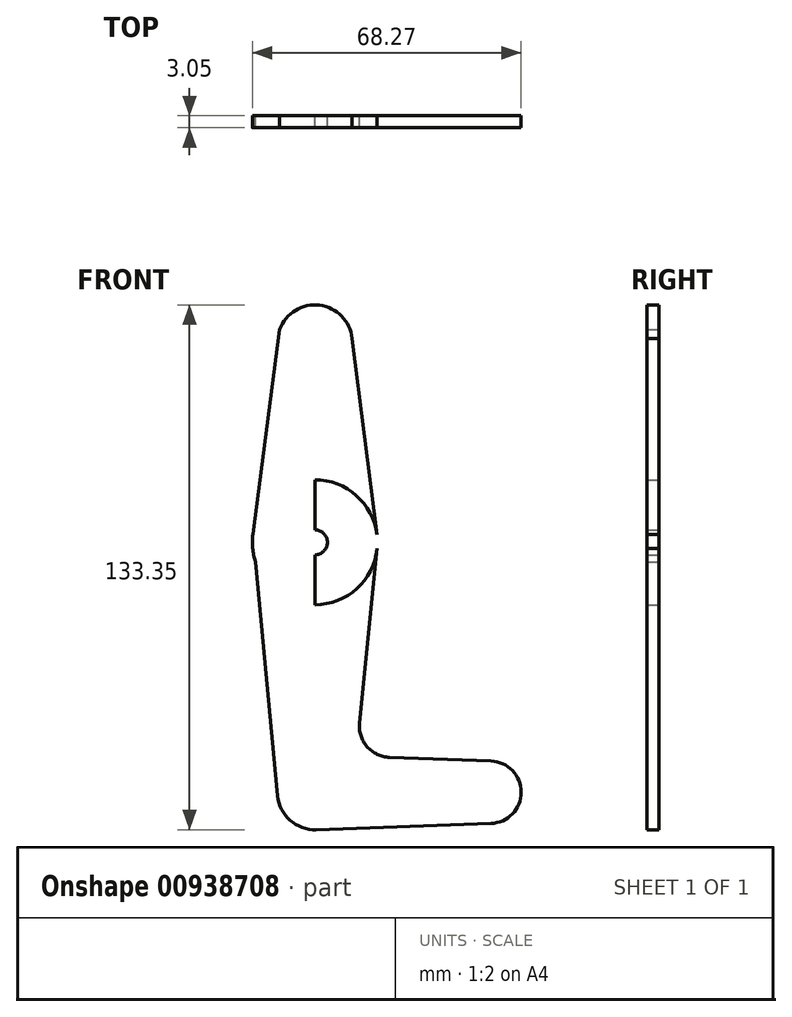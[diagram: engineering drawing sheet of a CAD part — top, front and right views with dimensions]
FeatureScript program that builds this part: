
annotation { "Feature Type Name" : "Feature", "Feature Type Description" : "" }
export const myFeature = defineFeature(function(context is Context, id is Id, definition is map)
    precondition{}
    {
        {
            var Q0;
            Q0=qCreatedBy(makeId("Front.planeOp"),FACE);
            var sketch = newSketch(context, id + "F0", { "sketchPlane" : qUnion([Q0])});
            skLineSegment(sketch, "E0", {"start": v(-32.72, 73.87) * mm, "end": v(-32.72, -40.43) * mm});
            skLineSegment(sketch, "E1", {"start": v(-32.72, -40.43) * mm, "end": v(11.73, -40.43) * mm});
            skCircle(sketch, "E2", {"center": v(-32.72, 73.87) * mm, "radius": 9.53 * mm});
            skCircle(sketch, "E3", {"center": v(-32.72, 23.07) * mm, "radius": 15.88 * mm});
            skCircle(sketch, "E4", {"center": v(-32.72, -40.43) * mm, "radius": 9.53 * mm});
            skCircle(sketch, "E5", {"center": v(11.73, -40.43) * mm, "radius": 7.94 * mm});
            skLineSegment(sketch, "E6", {"start": v(-16.92, 21.48) * mm, "end": v(-21.38, -22.84) * mm});
            skLineSegment(sketch, "E7", {"start": v(-32.38, -49.95) * mm, "end": v(12.01, -48.37) * mm});
            skLineSegment(sketch, "E8", {"start": v(-41.65, 77.18) * mm, "end": v(-48.46, 25.13) * mm});
            skLineSegment(sketch, "E9", {"start": v(-48.46, 25.13) * mm, "end": v(-42.2, -41.33) * mm});
            skLineSegment(sketch, "E10", {"start": v(-23.25, 74.86) * mm, "end": v(-16.97, 25.05) * mm});
            skLineSegment(sketch, "E11", {"start": v(-13.75, -31.58) * mm, "end": v(12.01, -32.5) * mm});
            skArc(sketch, "E12.filletArc", {"start": v(-21.38, -22.84) * mm, "mid": v(-19.46, -28.86) * mm, "end": v(-13.75, -31.58) * mm});
            skCircle(sketch, "E13", {"center": v(-32.72, 73.87) * mm, "radius": 3.18 * mm});
            skCircle(sketch, "E14", {"center": v(-32.72, 23.07) * mm, "radius": 3.18 * mm});
            skCircle(sketch, "E15", {"center": v(-32.72, -40.43) * mm, "radius": 3.18 * mm});
            skCircle(sketch, "E16", {"center": v(11.73, -40.43) * mm, "radius": 3.17 * mm});
            skCircle(sketch, "E17", {"center": v(-35.9, 59.6) * mm, "radius": 3.18 * mm});
            skSolve(sketch);
        }
        {
            var Q0;
            {var subQ0=sQuery(id+"F0.wireOp",EDGE,"E4");var subQ3=sQuery(id+"F0.wireOp",EDGE,"E0");var subQ4=makeQuery(id+"F0.imprint","INTERSECT",VERTEX,{"derivedFrom":[subQ3,subQ0]});Q0=makeQuery(id+"F0.imprint","IMPRINT",FACE,{"disambiguationData":[TD([[makeQuery(id+"F0.imprint","IMPRINT",EDGE,{"disambiguationData":[TD([[subQ4,-1.0]])],"derivedFrom":subQ3}),-1.0]])]});}
            var Q1;
            {var subQ0=sQuery(id+"F0.wireOp",EDGE,"E1");var subQ1=sQuery(id+"F0.wireOp",EDGE,"E0");var subQ2=makeQuery(id+"F0.imprint","INTERSECT",VERTEX,{"derivedFrom":[subQ1,subQ0]});Q1=makeQuery(id+"F0.imprint","IMPRINT",FACE,{"disambiguationData":[TD([[makeQuery(id+"F0.imprint","IMPRINT",EDGE,{"disambiguationData":[TD([[subQ2,1.0]])],"derivedFrom":subQ1}),1.0]])]});}
            var Q2;
            {var subQ5=sQuery(id+"F0.wireOp",EDGE,"E7");Q2=makeQuery(id+"F0.imprint","IMPRINT",FACE,{"disambiguationData":[TD([[makeQuery(id+"F0.imprint","IMPRINT",EDGE,{"derivedFrom":subQ5}),1.0]])]});}
            var Q3;
            {var subQ1=sQuery(id+"F0.wireOp",EDGE,"E3");var subQ3=sQuery(id+"F0.wireOp",EDGE,"E0");var subQ6=makeQuery(id+"F0.imprint","INTERSECT",VERTEX,{"disambiguationData":[OD(0.0)],"derivedFrom":[subQ3,subQ1]});Q3=makeQuery(id+"F0.imprint","IMPRINT",FACE,{"disambiguationData":[TD([[makeQuery(id+"F0.imprint","IMPRINT",EDGE,{"disambiguationData":[TD([[subQ6,-1.0]])],"derivedFrom":subQ3}),-1.0]])]});}
            var Q4;
            {var subQ0=sQuery(id+"F0.wireOp",EDGE,"E14");var subQ1=sQuery(id+"F0.wireOp",EDGE,"E0");var subQ2=makeQuery(id+"F0.imprint","INTERSECT",VERTEX,{"disambiguationData":[OD(0.0)],"derivedFrom":[subQ1,subQ0]});Q4=makeQuery(id+"F0.imprint","IMPRINT",FACE,{"disambiguationData":[TD([[makeQuery(id+"F0.imprint","IMPRINT",EDGE,{"disambiguationData":[TD([[subQ2,-1.0]])],"derivedFrom":subQ1}),1.0]])]});}
            var Q5;
            Q5=makeQuery(id+"F0.imprint","IMPRINT",FACE,{"disambiguationData":[TD([[makeQuery(id+"F0.imprint","IMPRINT",EDGE,{"derivedFrom":sQuery(id+"F0.wireOp",EDGE,"E17")}),1.0]])]});
            var Q6;
            {var subQ0=sQuery(id+"F0.wireOp",EDGE,"E3");var subQ2=sQuery(id+"F0.wireOp",EDGE,"E0");var subQ3=makeQuery(id+"F0.imprint","INTERSECT",VERTEX,{"disambiguationData":[OD(0.0)],"derivedFrom":[subQ2,subQ0]});Q6=makeQuery(id+"F0.imprint","IMPRINT",FACE,{"disambiguationData":[TD([[makeQuery(id+"F0.imprint","IMPRINT",EDGE,{"disambiguationData":[TD([[subQ3,-1.0]])],"derivedFrom":subQ2}),1.0]])]});}
            var Q7;
            {var subQ7=sQuery(id+"F0.wireOp",EDGE,"E6");Q7=makeQuery(id+"F0.imprint","IMPRINT",FACE,{"disambiguationData":[TD([[makeQuery(id+"F0.imprint","IMPRINT",EDGE,{"derivedFrom":subQ7}),-1.0]])]});}
            var Q8;
            {var subQ8=sQuery(id+"F0.wireOp",EDGE,"E17");Q8=makeQuery(id+"F0.imprint","IMPRINT",FACE,{"disambiguationData":[TD([[makeQuery(id+"F0.imprint","IMPRINT",EDGE,{"derivedFrom":subQ8}),-1.0]])]});}
            var Q9;
            Q9=makeQuery(id+"F0.imprint","IMPRINT",FACE,{"disambiguationData":[TD([[makeQuery(id+"F0.imprint","IMPRINT",EDGE,{"derivedFrom":sQuery(id+"F0.wireOp",EDGE,"E13")}),1.0]])]});
            var Q10;
            {var subQ0=sQuery(id+"F0.wireOp",EDGE,"E3");var subQ1=sQuery(id+"F0.wireOp",EDGE,"E0");var subQ2=makeQuery(id+"F0.imprint","INTERSECT",VERTEX,{"disambiguationData":[OD(1.0)],"derivedFrom":[subQ1,subQ0]});Q10=makeQuery(id+"F0.imprint","IMPRINT",FACE,{"disambiguationData":[TD([[makeQuery(id+"F0.imprint","IMPRINT",EDGE,{"disambiguationData":[TD([[subQ2,-1.0]])],"derivedFrom":subQ1}),-1.0]])]});}
            var Q11;
            {var subQ0=sQuery(id+"F0.wireOp",EDGE,"E14");var subQ1=sQuery(id+"F0.wireOp",EDGE,"E0");var subQ2=makeQuery(id+"F0.imprint","INTERSECT",VERTEX,{"disambiguationData":[OD(0.0)],"derivedFrom":[subQ1,subQ0]});Q11=makeQuery(id+"F0.imprint","IMPRINT",FACE,{"disambiguationData":[TD([[makeQuery(id+"F0.imprint","IMPRINT",EDGE,{"disambiguationData":[TD([[subQ2,-1.0]])],"derivedFrom":subQ1}),-1.0]])]});}
            var Q12;
            Q12=makeQuery(id+"F0.imprint","IMPRINT",FACE,{"disambiguationData":[TD([[makeQuery(id+"F0.imprint","IMPRINT",EDGE,{"derivedFrom":sQuery(id+"F0.wireOp",EDGE,"E16")}),-1.0]])]});
            var Q13;
            Q13=makeQuery(id+"F0.imprint","IMPRINT",FACE,{"disambiguationData":[TD([[makeQuery(id+"F0.imprint","IMPRINT",EDGE,{"derivedFrom":sQuery(id+"F0.wireOp",EDGE,"E16")}),1.0]])]});
            var Q14;
            {var subQ0=sQuery(id+"F0.wireOp",EDGE,"E4");var subQ1=sQuery(id+"F0.wireOp",EDGE,"E0");var subQ2=makeQuery(id+"F0.imprint","INTERSECT",VERTEX,{"derivedFrom":[subQ1,subQ0]});Q14=makeQuery(id+"F0.imprint","IMPRINT",FACE,{"disambiguationData":[TD([[makeQuery(id+"F0.imprint","IMPRINT",EDGE,{"disambiguationData":[TD([[subQ2,-1.0]])],"derivedFrom":subQ1}),1.0]])]});}
            var Q15;
            {var subQ0=sQuery(id+"F0.wireOp",EDGE,"E1");var subQ1=sQuery(id+"F0.wireOp",EDGE,"E0");var subQ2=makeQuery(id+"F0.imprint","INTERSECT",VERTEX,{"derivedFrom":[subQ1,subQ0]});Q15=makeQuery(id+"F0.imprint","IMPRINT",FACE,{"disambiguationData":[TD([[makeQuery(id+"F0.imprint","IMPRINT",EDGE,{"disambiguationData":[TD([[subQ2,1.0]])],"derivedFrom":subQ1}),-1.0]])]});}
            var Q16;
            Q16=makeQuery(id+"F0.imprint","IMPRINT",FACE,{"disambiguationData":[TD([[makeQuery(id+"F0.imprint","IMPRINT",EDGE,{"derivedFrom":sQuery(id+"F0.wireOp",EDGE,"E13")}),-1.0]])]});
            var Q17;
            {var subQ0=sQuery(id+"F0.wireOp",EDGE,"E10");Q17=makeQuery(id+"F0.imprint","IMPRINT",FACE,{"disambiguationData":[TD([[makeQuery(id+"F0.imprint","IMPRINT",EDGE,{"derivedFrom":subQ0}),-1.0]])]});}
            var Q18;
            {var subQ0=sQuery(id+"F0.wireOp",EDGE,"E9");var subQ1=sQuery(id+"F0.wireOp",EDGE,"E3");var subQ3=makeQuery(id+"F0.imprint","INTERSECT",VERTEX,{"derivedFrom":[subQ1,subQ0]});Q18=makeQuery(id+"F0.imprint","IMPRINT",FACE,{"disambiguationData":[TD([[makeQuery(id+"F0.imprint","IMPRINT",EDGE,{"disambiguationData":[TD([[subQ3,1.0]])],"derivedFrom":subQ1}),1.0]])]});}
            var Q19;
            {var subQ0=sQuery(id+"F0.wireOp",EDGE,"E8");var subQ1=sQuery(id+"F0.wireOp",EDGE,"E2");var subQ2=makeQuery(id+"F0.imprint","INTERSECT",VERTEX,{"disambiguationData":[OD(0.0)],"derivedFrom":[subQ1,subQ0]});Q19=makeQuery(id+"F0.imprint","IMPRINT",FACE,{"disambiguationData":[TD([[makeQuery(id+"F0.imprint","IMPRINT",EDGE,{"disambiguationData":[TD([[subQ2,-1.0]])],"derivedFrom":subQ1}),1.0]])]});}
            extrude(context, id + "F1", {"entities" : qUnion([Q0, Q1, Q2, Q3, Q4, Q5, Q6, Q7, Q8, Q9, Q10, Q11, Q12, Q13, Q14, Q15, Q16, Q17, Q18, Q19]), "depth" : 3.05 * mm, "offsetDistance" : 25.4 * mm});
        }
    });
